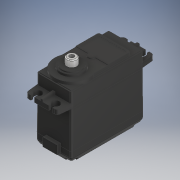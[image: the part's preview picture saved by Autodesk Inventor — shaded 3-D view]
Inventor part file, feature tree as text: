
AUTODESK INVENTOR PART (.ipt)
format: ipt  version: 2019.4 (Build 234330000, 330)  size: 534,528 bytes
history: native  units: mm
features: sketch x19, extrude x14, projected_geometry x13, other x8, chamfer x5, fillet x4, mirror x3, hole x2, loft x1
ambient origin geometry x8: Origin, YZ Plane, XZ Plane, XY Plane, X Axis, Y Axis, Z Axis, Center Point
bodies: Body1 (feature_tree), Body2 (feature_tree)
feature tree (69):
  other  "ソリッド1"
  extrude  "押し出し1"  Depth=40.7mm
  sketch  "スケッチ2"
  other  "作業平面1"
  loft  "ロフト1"
  extrude  "押し出し2"  Depth=6.5mm TaperAngle=0.0deg
  sketch  "スケッチ5"
  extrude  "押し出し3"  Depth=20.5mm
  other  "作業平面2"
  extrude  "押し出し4"  Depth=40.4mm
  other  "作業平面3"
  mirror  "ミラー1"
  fillet  "フィレット2"  Radius=19.5mm
  chamfer  "面取り1"  Angle=90.0deg  [1 undecoded]
  chamfer  "面取り2"  Angle=90.0deg  [1 undecoded]
  chamfer  "面取り3"  Distance=40.25mm
  chamfer  "面取り4"  Distance=19.3mm
  extrude  "押し出し5"  Depth=8.2mm TaperAngle=0.0deg
  hole  "穴1"  [1 undecoded]
  mirror  "ミラー2"
  mirror  "ミラー3"
  fillet  "フィレット3"  Radius=19.3mm
  fillet  "フィレット4"  Radius=0.25mm
  extrude  "押し出し6"  Depth=7.2mm
  extrude  "押し出し7"  Depth=10.0mm
  fillet  "フィレット5"  Radius=4.2mm
  extrude  "押し出し8"  Depth=4.2mm
  extrude  "押し出し9"  Depth=2.0mm
  extrude  "押し出し10"  Depth=1.0mm
  hole  "穴2"  [1 undecoded]
  chamfer  "面取り5"  Distance=1.0mm
  extrude  "押し出し11"  Depth=6.875mm
  extrude  "押し出し12"  Depth=2.5mm TaperAngle=0.0deg
  extrude  "押し出し13"  Depth=1.2mm
  other  "作業平面5"
  extrude  "押し出し14"  Depth=1.7mm
  sketch  "スケッチ1"
  projected_geometry  "投影ループ1"
  sketch  "スケッチ3"
  projected_geometry  "投影ループ2"
  other  "エッジ1"
  sketch  "スケッチ4"
  sketch  "スケッチ6"
  projected_geometry  "投影ループ3"
  sketch  "スケッチ7"
  projected_geometry  "投影ループ4"
  projected_geometry  "投影ループ5"
  other  "作業平面4"
  sketch  "スケッチ8"
  projected_geometry  "投影ループ6"
  sketch  "スケッチ9"
  sketch  "スケッチ10"
  projected_geometry  "投影ループ7"
  sketch  "スケッチ11"
  sketch  "スケッチ12"
  projected_geometry  "投影ループ8"
  sketch  "スケッチ14"
  sketch  "スケッチ15"
  other  "ソリッド2"
  sketch  "スケッチ16"
  sketch  "スケッチ18"
  projected_geometry  "投影ループ9"
  sketch  "スケッチ19"
  projected_geometry  "投影ループ10"
  projected_geometry  "投影ループ11"
  sketch  "スケッチ20"
  projected_geometry  "投影ループ12"
  sketch  "スケッチ21"
  projected_geometry  "投影ループ13"
note: 4 required parameter values undecoded (feature->parameter linkage not recoverable at this tier; creation-order binding heuristic only, values carry confidence <= 0.55)
